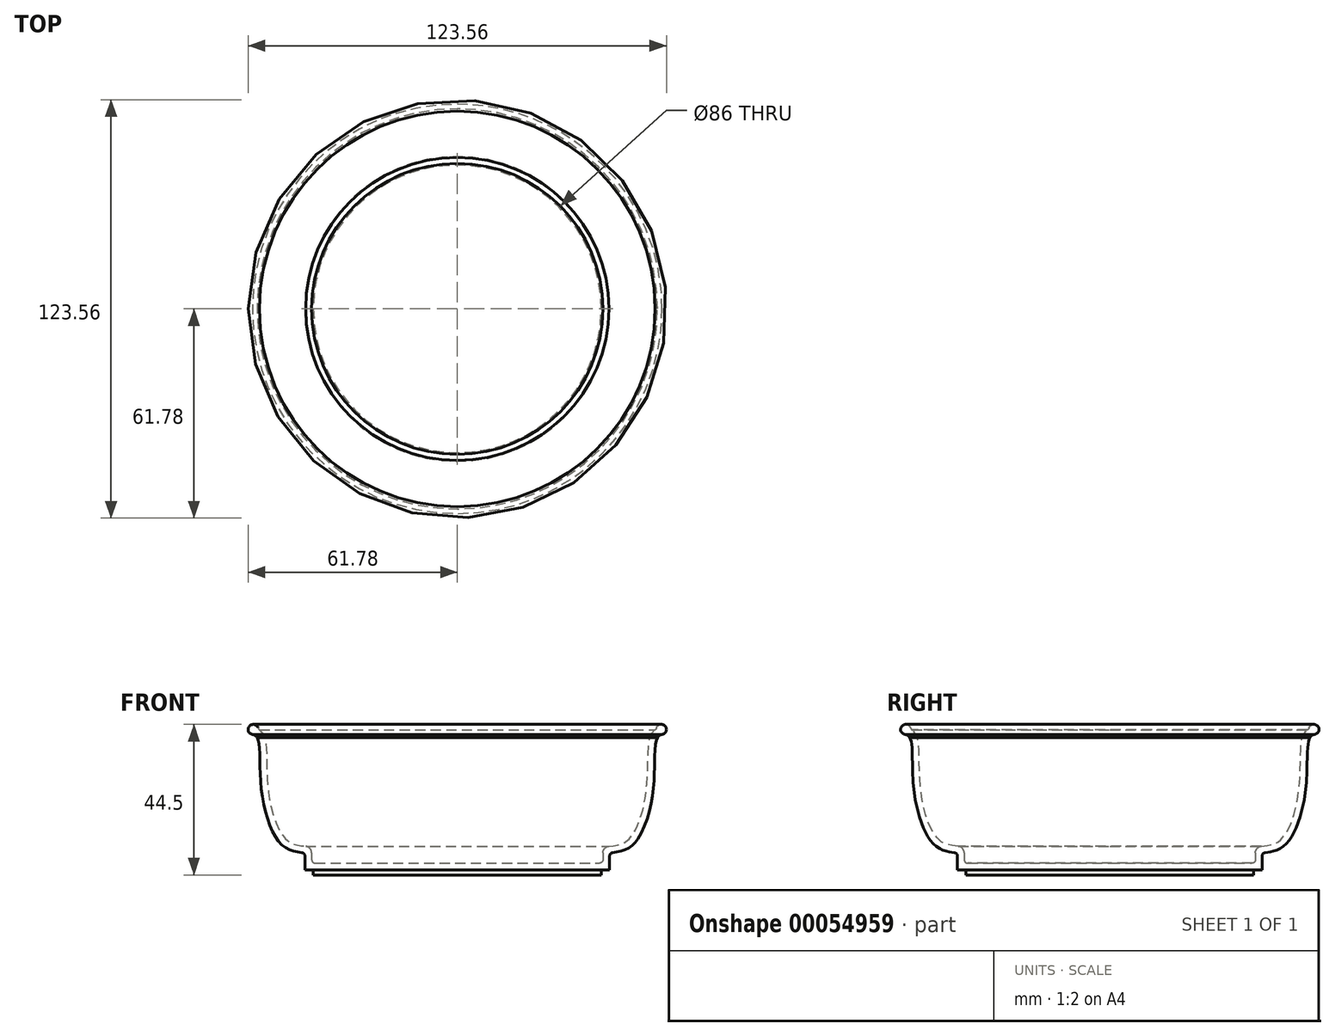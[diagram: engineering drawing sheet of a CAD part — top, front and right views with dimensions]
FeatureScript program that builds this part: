
annotation { "Feature Type Name" : "Feature", "Feature Type Description" : "" }
export const myFeature = defineFeature(function(context is Context, id is Id, definition is map)
    precondition{}
    {
        {
            var Q0;
            Q0=qCreatedBy(makeId("Front.planeOp"),FACE);
            var sketch = newSketch(context, id + "F0", { "sketchPlane" : qUnion([Q0])});
            skLineSegment(sketch, "E0", {"start": v(0, 0) * mm, "end": v(45, 0) * mm});
            skLineSegment(sketch, "E1", {"start": v(45, 0) * mm, "end": v(45, 4.1) * mm});
            skPoint(sketch, "E2", {"position": v(51.76, 7.36) * mm});
            skPoint(sketch, "E3", {"position": v(57.83, 23.5) * mm});
            skPoint(sketch, "E4", {"position": v(58.8, 38.41) * mm});
            skFitSpline(sketch, "E5", {"points": [v(60, 40) * mm, v(58.8, 38.41) * mm, v(57.83, 23.5) * mm, v(51.76, 7.36) * mm, v(45, 5) * mm], "startDerivative": vector(-11.79, -9.17) * mm, "endDerivative": vector(-32.3, -3.58) * mm});
            skLineSegment(sketch, "E6", {"start": v(0, 0) * mm, "end": v(0, 41.8) * mm, "construction": true});
            skLineSegment(sketch, "E7.0", {"start": v(43, 2) * mm, "end": v(43, 5) * mm});
            skLineSegment(sketch, "E7.1", {"start": v(0, 2) * mm, "end": v(43, 2) * mm});
            skArc(sketch, "E8", {"start": v(43, 5) * mm, "mid": v(43.5, 6.33) * mm, "end": v(44.78, 6.99) * mm});
            skFitSpline(sketch, "E9.0", {"points": [v(58.77, 41.58) * mm, v(58.65, 41.48) * mm, v(58.33, 41.24) * mm, v(57.83, 40.75) * mm, v(57.45, 40.22) * mm, v(57.19, 39.77) * mm, v(56.97, 39.28) * mm, v(56.8, 38.74) * mm, v(56.68, 38.2) * mm, v(56.55, 37.46) * mm, v(56.45, 36.47) * mm, v(56.37, 35.16) * mm, v(56.3, 33.25) * mm, v(56.26, 30.61) * mm, v(56.17, 27.74) * mm, v(56.02, 25.4) * mm, v(55.85, 23.64) * mm, v(55.6, 21.89) * mm, v(55.2, 19.59) * mm, v(54.54, 16.8) * mm, v(53.52, 13.79) * mm, v(52.52, 11.66) * mm, v(51.66, 10.28) * mm, v(51.12, 9.57) * mm, v(50.68, 9.09) * mm, v(50.36, 8.78) * mm, v(50.05, 8.52) * mm, v(49.62, 8.21) * mm, v(49.06, 7.9) * mm, v(48.1, 7.52) * mm, v(46.73, 7.2) * mm, v(45.45, 7.06) * mm, v(44.78, 6.99) * mm]});
            skArc(sketch, "E10.filletArc", {"start": v(45.88, 5.1) * mm, "mid": v(45.25, 4.77) * mm, "end": v(45, 4.1) * mm});
            skArc(sketch, "E11", {"start": v(60.48, 40.01) * mm, "mid": v(61.44, 42.44) * mm, "end": v(58.87, 42.02) * mm});
            skArc(sketch, "E12.filletArc", {"start": v(60.48, 40.01) * mm, "mid": v(59.7, 39.7) * mm, "end": v(59.12, 39.1) * mm});
            skArc(sketch, "E13.filletArc", {"start": v(58.32, 41.2) * mm, "mid": v(58.64, 41.58) * mm, "end": v(58.87, 42.02) * mm});
            skLineSegment(sketch, "E14", {"start": v(0, 0) * mm, "end": v(0, 2) * mm});
            skSolve(sketch);
        }
        {
            var Q0;
            Q0=qSketchRegion(id+"F0",true);
            var Q1;
            Q1=sQuery(id+"F0.wireOp",EDGE,"E5");
            var Q2;
            Q2=sQuery(id+"F0.wireOp",EDGE,"E1");
            var Q3;
            Q3=sQuery(id+"F0.wireOp",EDGE,"E0");
            var Q4;
            Q4=sQuery(id+"F0.wireOp",EDGE,"E7.1");
            var Q5;
            Q5=sQuery(id+"F0.wireOp",EDGE,"E7.0");
            var Q6;
            Q6=sQuery(id+"F0.wireOp",EDGE,"E8");
            var Q7;
            Q7=sQuery(id+"F0.wireOp",EDGE,"E9.0");
            var Q8;
            Q8=sQuery(id+"F0.wireOp",EDGE,"E6");
            revolve(context, id + "F1", {"entities" : qUnion([Q0]), "surfaceEntities" : qUnion([Q1, Q2, Q3, Q4, Q5, Q6, Q7]), "axis" : qUnion([Q8]), "revolveType" : RevolveType.FULL});
        }
        {
            var Q0;
            Q0=makeQuery(id+"F1.opRevolve","SWEPT_EDGE",EDGE,{"disambiguationData":[OSD([sQuery(id+"F0.wireOp",EDGE,"E7.0"),sQuery(id+"F0.wireOp",EDGE,"E7.1")])]});
            fillet(context, id + "F2", {"entities" : qUnion([Q0]), "radius" : 1 * mm, "tangentPropagation" : true, "allowEdgeOverflow" : false});
        }
        {
            var Q0;
            Q0=makeQuery(id+"F1.opRevolve","SWEPT_FACE",FACE,{"disambiguationData":[OSD([sQuery(id+"F0.wireOp",EDGE,"E0")])]});
            var sketch = newSketch(context, id + "F3", { "sketchPlane" : qUnion([Q0])});
            skCircle(sketch, "E15", {"center": v(0, 0) * mm, "radius": 42.5 * mm});
            skSolve(sketch);
        }
        {
            var Q0;
            Q0=qSketchRegion(id+"F3",true);
            extrude(context, id + "F4", {"entities" : qUnion([Q0]), "operationType" : NewBodyOperationType.ADD, "depth" : 1.5 * mm});
        }
    });
